AUTODESK INVENTOR PART (.ipt)
format: ipt  version: 2017 SP1 (Build 210196100, 196)  size: 125,952 bytes
history: native  units: in
note: dims shown in document units (in); Inventor stores cm internally (conversion verified against a paired STEP export)
features: sketch x1
ambient origin geometry x8: Origin, YZ Plane, XZ Plane, XY Plane, X Axis, Y Axis, Z Axis, Center Point
feature tree (1):
  sketch  "Sketch1"  dims[d0=5.0in d1=2.0in d3=1.0in d4=7.5in d5=7.5in d7=10.75in d10=1.25in d11=3.25in d16=14.0in d21=8.0in d38=14.0in d39=52.0in d40=66.0in d41=3.0in d42=12.0in d43=55.0in d45=1.0in d46=1.0in d47=18.0in d48=8.0in]
